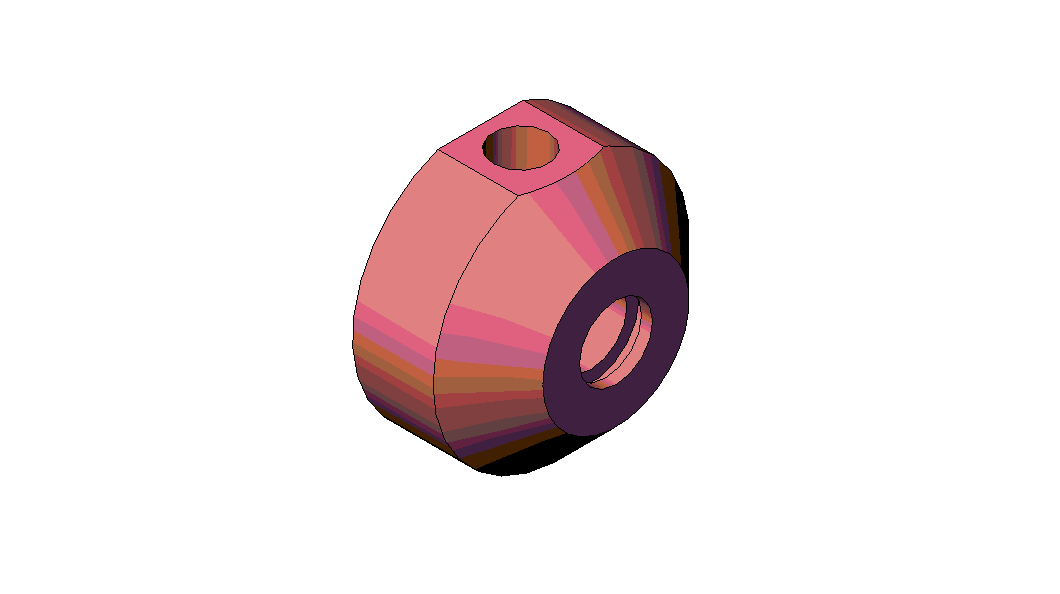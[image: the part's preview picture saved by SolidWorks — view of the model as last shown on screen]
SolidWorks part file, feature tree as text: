
SOLIDWORKS PART (.sldprt)
format: sldprt  version: not decoded by parser v0  size: 210,432 bytes
history: native  units: mm
features: sketch x6, cut_extrude x5, plane x4, material x1, revolve x1, pattern_circular x1 + 1 further entry (+7 scaffold rows collapsed)
feature tree (26):
  scaffold x7  (default folders/planes/origin — collapsed)
  material  "Matériau <non spécifié>"
  "Corps de surface"
  plane  "Plan1"
  plane  "Plan2"
  plane  "Plan3"
  sketch  "Esquisse1"  dims[c1.D1=20.0mm c1.D2=13.0mm c1.D3=~2.828427mm c2.D3=45.0deg c2.D4=3.0mm c2.D5=3.0mm c2.D6=2.6mm c2.D7=10.0mm c2.D8=22.0mm c2.D9=~14.866069mm c3.D9=45.0deg c3.D10=47.0mm c3.D11=18.5mm c3.D12=3.0mm c3.D13=4.0mm c3.D14=10.0mm c3.D15=13.25mm c3.D16=28.0mm c3.D2=13.0mm c3.D3=35.0mm c3.D17=~12.369317mm c4.D17=45.0deg c4.D18=~3.162278mm c5.D18=60.0deg]
  revolve  "Base-Révolution"  Angle=360deg
  sketch  "Esquisse2"  dims[D1=33.0mm]
  cut_extrude  "Enlèv. mat.-Extru.1"  Depth=50mm
  sketch  "Esquisse3"  dims[D1=14.95mm D2=11.0mm]
  cut_extrude  "Enlèv. mat.-Extru.2"  [1 undecoded]
  sketch  "Esquisse4"  dims[c1.D2=6.0mm c1.D1=39.0mm c2.D1=45.0deg c2.D3=28.0mm]
  cut_extrude  "Enlèv. mat.-Extru.3"  Depth=20mm
  pattern_circular  "Répétition circulaire1"  Count=4 Angle=90deg
  plane  "Plan4"  Offset=35mm
  sketch  "Esquisse7"  dims[D1=6.0mm D2=11.0mm]
  cut_extrude  "Enlèv. mat.-Extru.5"  Depth=11mm
  sketch  "Esquisse8"  dims[D1=2.0mm]
  cut_extrude  "Enlèv. mat.-Extru.6"  [1 undecoded]
decode coverage: 11 of 13 modeling features carry decoded parameters; 1 rows unclassified (native names shown)
note: ~ marks probable driven/reference dimensions
note: 2 parameter values undecoded
note: suppression state not decoded; provenance and decode notes live in map.json
